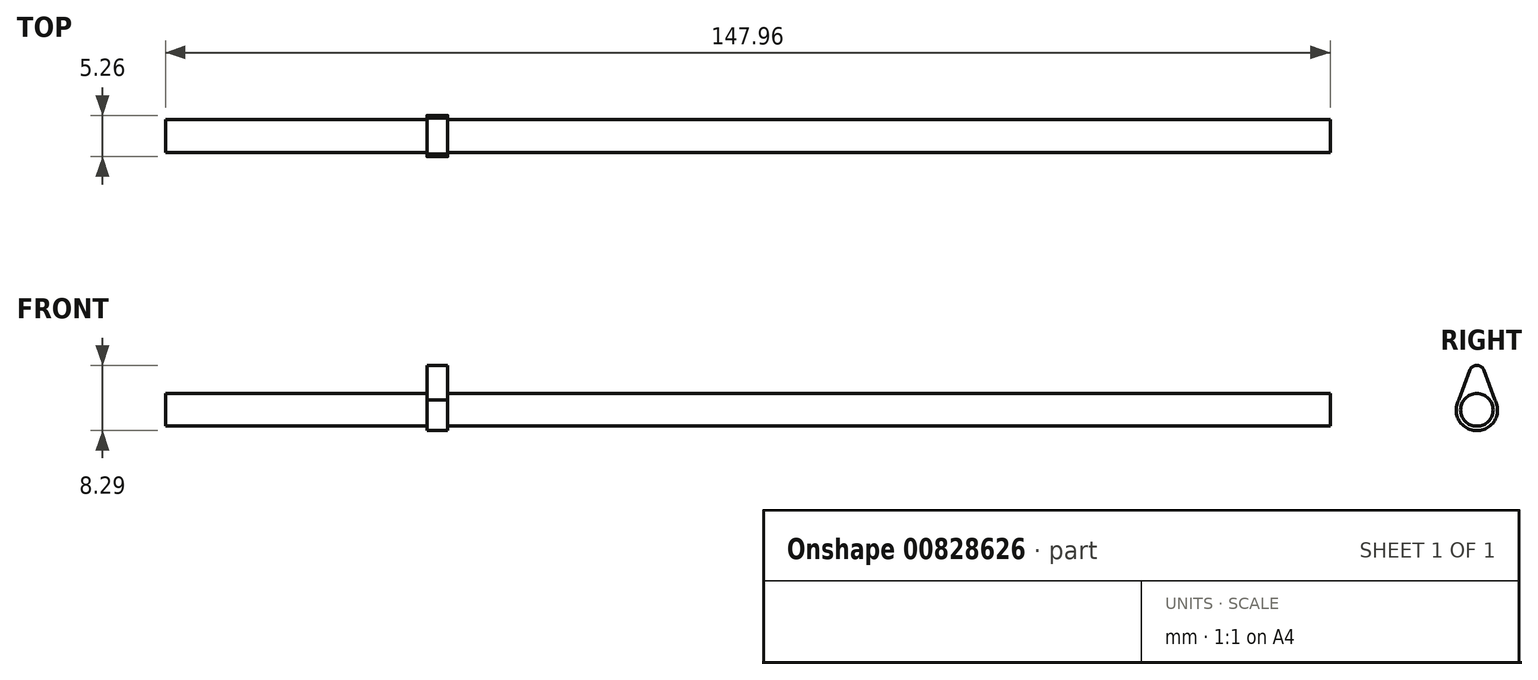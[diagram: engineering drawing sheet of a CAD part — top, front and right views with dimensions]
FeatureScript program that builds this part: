
annotation { "Feature Type Name" : "Feature", "Feature Type Description" : "" }
export const myFeature = defineFeature(function(context is Context, id is Id, definition is map)
    precondition{}
    {
        {
            var Q0;
            Q0=qCreatedBy(makeId("Right.planeOp"),FACE);
            var sketch = newSketch(context, id + "F0", { "sketchPlane" : qUnion([Q0])});
            skCircle(sketch, "E0", {"center": v(0, 0) * mm, "radius": 2.07 * mm});
            skSolve(sketch);
        }
        {
            var Q0;
            Q0 = qSketchRegion(id + "F0", true);
            extrude(context, id + "F1", {"entities" : qUnion([Q0]), "endBound" : BoundingType.SYMMETRIC, "depth" : 147.95 * mm, "offsetDistance" : 25.4 * mm});
        }
        {
            var Q0;
            Q0=qCreatedBy(makeId("Right.planeOp"),FACE);
            var sketch = newSketch(context, id + "F2", { "sketchPlane" : qUnion([Q0])});
            skCircle(sketch, "E1", {"center": v(0, 0) * mm, "radius": 2.63 * mm});
            skCircle(sketch, "E2", {"center": v(0, 4.73) * mm, "radius": 0.93 * mm});
            skLineSegment(sketch, "E3", {"start": v(-2.31, 1.25) * mm, "end": v(-0.87, 5.06) * mm});
            skLineSegment(sketch, "E4.MirrorCS", {"start": v(2.31, 1.25) * mm, "end": v(0.87, 5.06) * mm});
            skSolve(sketch);
        }
        {
            var Q0;
            Q0 = qSketchRegion(id + "F2", true);
            extrude(context, id + "F3", {"entities" : qUnion([Q0]), "operationType" : NewBodyOperationType.ADD, "oppositeDirection" : true, "depth" : 73.96 * mm, "offsetDistance" : 25.4 * mm});
        }
        {
            var Q0;
            Q0=qCreatedBy(makeId("Right.planeOp"),FACE);
            var sketch = newSketch(context, id + "F4", { "sketchPlane" : qUnion([Q0])});
            skSolve(sketch);
        }
        {
            var Q0;
            Q0 = qSketchRegion(id + "F4", true);
            var Q1;
            Q1=makeQuery(id+"F3.opExtrude","CAP_FACE",FACE,{"disambiguationData":[OSD([sQuery(id+"F2.wireOp",EDGE,"E1"),sQuery(id+"F2.wireOp",EDGE,"E2"),sQuery(id+"F2.wireOp",EDGE,"E3"),sQuery(id+"F2.wireOp",EDGE,"E4.MirrorCS")])],"isStart":false});
            extrude(context, id + "F5", {"entities" : qUnion([Q0, Q1]), "operationType" : NewBodyOperationType.REMOVE, "oppositeDirection" : true, "depth" : 33.2 * mm, "offsetDistance" : 25.4 * mm});
        }
        {
            var Q0;
            Q0=makeQuery(id+"F3.opExtrude","CAP_FACE",FACE,{"disambiguationData":[OSD([sQuery(id+"F2.wireOp",EDGE,"E1"),sQuery(id+"F2.wireOp",EDGE,"E2"),sQuery(id+"F2.wireOp",EDGE,"E3"),sQuery(id+"F2.wireOp",EDGE,"E4.MirrorCS")])],"isStart":true});
            extrude(context, id + "F6", {"entities" : qUnion([Q0]), "operationType" : NewBodyOperationType.REMOVE, "oppositeDirection" : true, "depth" : 38.1 * mm, "offsetDistance" : 25.4 * mm});
        }
    });
